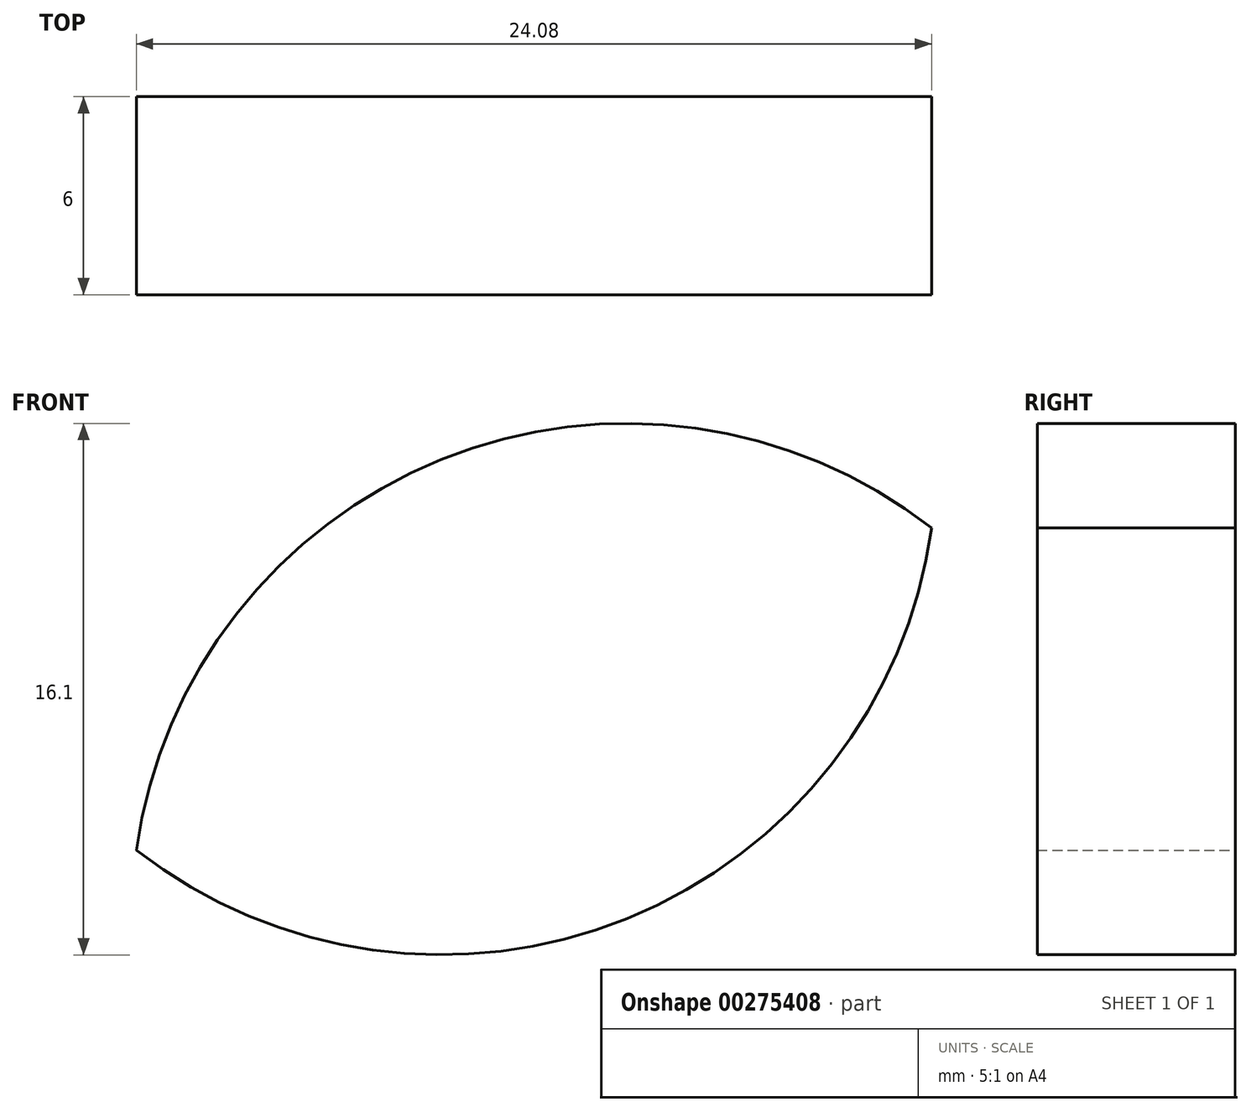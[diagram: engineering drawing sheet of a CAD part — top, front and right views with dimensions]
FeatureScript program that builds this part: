
annotation { "Feature Type Name" : "Feature", "Feature Type Description" : "" }
export const myFeature = defineFeature(function(context is Context, id is Id, definition is map)
    precondition{}
    {
        {
            var Q0;
            Q0=qCreatedBy(makeId("Front.planeOp"),FACE);
            var sketch = newSketch(context, id + "F0", { "sketchPlane" : qUnion([Q0])});
            skArc(sketch, "E0", {"start": v(-40.5, 14.72) * mm, "mid": v(-55.36, 16.8) * mm, "end": v(-64.58, 4.96) * mm});
            skArc(sketch, "E1", {"start": v(-64.58, 4.96) * mm, "mid": v(-49.72, 2.9) * mm, "end": v(-40.5, 14.72) * mm});
            skSolve(sketch);
        }
        {
            var Q0;
            Q0 = qSketchRegion(id + "F0", true);
            extrude(context, id + "F1", {"entities" : qUnion([Q0]), "depth" : 6 * mm, "offsetDistance" : 25 * mm});
        }
    });
